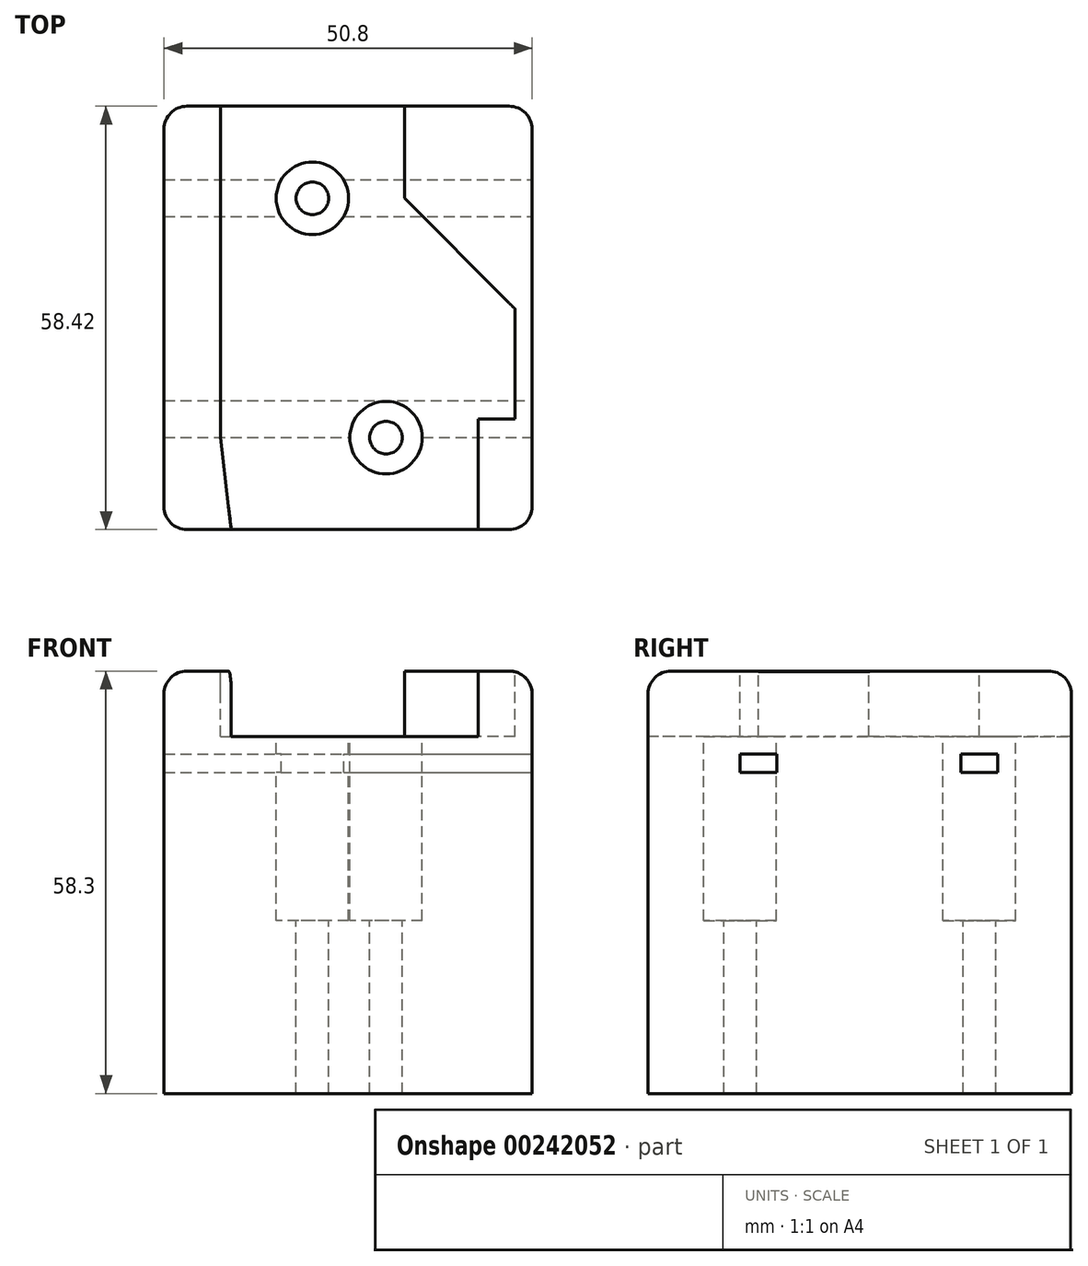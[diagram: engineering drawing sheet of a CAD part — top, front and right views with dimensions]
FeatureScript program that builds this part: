
annotation { "Feature Type Name" : "Feature", "Feature Type Description" : "" }
export const myFeature = defineFeature(function(context is Context, id is Id, definition is map)
    precondition{}
    {
        {
            var Q0;
            Q0=qCreatedBy(makeId("Top.planeOp"),FACE);
            var sketch = newSketch(context, id + "F0", { "sketchPlane" : qUnion([Q0])});
            skLineSegment(sketch, "E0.bottom", {"start": v(3.17, 58.42) * mm, "end": v(47.62, 58.42) * mm});
            skLineSegment(sketch, "E0.top", {"start": v(3.18, 0) * mm, "end": v(47.62, 0) * mm});
            skLineSegment(sketch, "E0.left", {"start": v(0, 55.24) * mm, "end": v(0, 3.17) * mm});
            skLineSegment(sketch, "E0.right", {"start": v(50.8, 55.24) * mm, "end": v(50.8, 3.17) * mm});
            skPoint(sketch, "E1.visualSharp", {"position": v(0, 58.42) * mm});
            skArc(sketch, "E1.filletArc", {"start": v(3.17, 58.42) * mm, "mid": v(0.93, 57.5) * mm, "end": v(0, 55.24) * mm});
            skPoint(sketch, "E2.visualSharp", {"position": v(50.8, 58.42) * mm});
            skArc(sketch, "E2.filletArc", {"start": v(50.8, 55.24) * mm, "mid": v(49.87, 57.5) * mm, "end": v(47.62, 58.42) * mm});
            skPoint(sketch, "E3.visualSharp", {"position": v(50.8, 0) * mm});
            skArc(sketch, "E3.filletArc", {"start": v(47.63, 0) * mm, "mid": v(49.87, 0.93) * mm, "end": v(50.8, 3.17) * mm});
            skPoint(sketch, "E4.visualSharp", {"position": v(0, 0) * mm});
            skArc(sketch, "E4.filletArc", {"start": v(0, 3.17) * mm, "mid": v(0.93, 0.93) * mm, "end": v(3.18, 0) * mm});
            skSolve(sketch);
        }
        {
            var Q0;
            Q0=makeQuery(id+"F0.imprint","IMPRINT",FACE,{"disambiguationData":[TD([[makeQuery(id+"F0.imprint","IMPRINT",EDGE,{"derivedFrom":sQuery(id+"F0.wireOp",EDGE,"E0.bottom")}),-1.0]])]});
            extrude(context, id + "F1", {"entities" : qUnion([Q0]), "depth" : 50.8 * mm + 7.5 * mm});
        }
        {
            var Q0;
            Q0=makeQuery(id+"F1.opExtrude","CAP_FACE",FACE,{"disambiguationData":[OSD([sQuery(id+"F0.wireOp",EDGE,"E0.bottom"),sQuery(id+"F0.wireOp",EDGE,"E0.top"),sQuery(id+"F0.wireOp",EDGE,"E0.left"),sQuery(id+"F0.wireOp",EDGE,"E0.right"),sQuery(id+"F0.wireOp",EDGE,"E1.filletArc"),sQuery(id+"F0.wireOp",EDGE,"E2.filletArc"),sQuery(id+"F0.wireOp",EDGE,"E3.filletArc"),sQuery(id+"F0.wireOp",EDGE,"E4.filletArc")])],"isStart":false});
            var sketch = newSketch(context, id + "F2", { "sketchPlane" : qUnion([Q0])});
            skLineSegment(sketch, "E5", {"start": v(33.18, 58.42) * mm, "end": v(33.18, 45.72) * mm});
            skLineSegment(sketch, "E6", {"start": v(33.18, 45.72) * mm, "end": v(48.42, 30.48) * mm});
            skLineSegment(sketch, "E7", {"start": v(48.42, 30.48) * mm, "end": v(48.42, 15.24) * mm});
            skLineSegment(sketch, "E8", {"start": v(48.42, 15.24) * mm, "end": v(43.34, 15.24) * mm});
            skLineSegment(sketch, "E9", {"start": v(43.34, 15.24) * mm, "end": v(43.34, 0) * mm});
            skLineSegment(sketch, "E10", {"start": v(43.34, 0) * mm, "end": v(7.78, 0) * mm});
            skLineSegment(sketch, "E11", {"start": v(7.78, 0) * mm, "end": v(7.78, 58.42) * mm});
            skLineSegment(sketch, "E12", {"start": v(7.78, 12.7) * mm, "end": v(9.28, 0) * mm});
            skSolve(sketch);
        }
        {
            var Q0;
            {var subQ0=sQuery(id+"F2.wireOp",EDGE,"E5");Q0=makeQuery(id+"F2.imprint","IMPRINT",FACE,{"disambiguationData":[TD([[makeQuery(id+"F2.imprint","IMPRINT",EDGE,{"derivedFrom":subQ0}),-1.0]])]});}
            extrude(context, id + "F3", {"entities" : qUnion([Q0]), "operationType" : NewBodyOperationType.REMOVE, "oppositeDirection" : true, "depth" : 9.02 * mm});
        }
        {
            var Q0;
            Q0=makeQuery(id+"F1.opExtrude","SWEPT_FACE",FACE,{"disambiguationData":[OSD([sQuery(id+"F0.wireOp",EDGE,"E0.right")])]});
            var sketch = newSketch(context, id + "F4", { "sketchPlane" : qUnion([Q0])});
            skLineSegment(sketch, "E13.bottom", {"start": v(12.7, 46.87) * mm, "end": v(17.78, 46.87) * mm});
            skLineSegment(sketch, "E13.top", {"start": v(12.7, 44.33) * mm, "end": v(17.78, 44.33) * mm});
            skLineSegment(sketch, "E13.left", {"start": v(12.7, 46.87) * mm, "end": v(12.7, 44.33) * mm});
            skLineSegment(sketch, "E13.right", {"start": v(17.78, 46.87) * mm, "end": v(17.78, 44.33) * mm});
            skLineSegment(sketch, "E14.bottom", {"start": v(43.18, 44.33) * mm, "end": v(48.26, 44.33) * mm});
            skLineSegment(sketch, "E14.top", {"start": v(43.18, 46.87) * mm, "end": v(48.26, 46.87) * mm});
            skLineSegment(sketch, "E14.left", {"start": v(43.18, 44.33) * mm, "end": v(43.18, 46.87) * mm});
            skLineSegment(sketch, "E14.right", {"start": v(48.26, 44.33) * mm, "end": v(48.26, 46.87) * mm});
            skSolve(sketch);
        }
        {
            var Q0;
            Q0 = qSketchRegion(id + "F4", true);
            extrude(context, id + "F5", {"entities" : qUnion([Q0]), "operationType" : NewBodyOperationType.REMOVE, "endBound" : BoundingType.THROUGH_ALL, "oppositeDirection" : true, "depth" : 25.4 * mm});
        }
        {
            var Q0;
            Q0=makeQuery(id+"F3.boolean.opBoolean","COPY",EDGE,{"derivedFrom":makeQuery(id+"F3.opExtrude","SWEPT_EDGE",EDGE,{"disambiguationData":[OSD([sQuery(id+"F0.wireOp",EDGE,"E0.top"),sQuery(id+"F2.wireOp",EDGE,"E10"),sQuery(id+"F2.wireOp",EDGE,"E11")])]})});
            var Q1;
            Q1=makeQuery(id+"F3.boolean.opBoolean","COPY",EDGE,{"derivedFrom":makeQuery(id+"F3.opExtrude","SWEPT_EDGE",EDGE,{"disambiguationData":[OSD([sQuery(id+"F0.wireOp",EDGE,"E0.top"),sQuery(id+"F2.wireOp",EDGE,"E9"),sQuery(id+"F2.wireOp",EDGE,"E10")])]})});
            var Q2;
            Q2=makeQuery(id+"F3.boolean.opBoolean","COPY",EDGE,{"derivedFrom":makeQuery(id+"F3.opExtrude","SWEPT_EDGE",EDGE,{"disambiguationData":[OSD([sQuery(id+"F0.wireOp",EDGE,"E0.bottom"),sQuery(id+"F2.wireOp",EDGE,"E11")])]})});
            var Q3;
            Q3=makeQuery(id+"F3.boolean.opBoolean","COPY",EDGE,{"derivedFrom":makeQuery(id+"F3.opExtrude","SWEPT_EDGE",EDGE,{"disambiguationData":[OSD([sQuery(id+"F0.wireOp",EDGE,"E0.bottom"),sQuery(id+"F2.wireOp",EDGE,"E5")])]})});
            var Q4;
            Q4=makeQuery(id+"F1.opExtrude","CAP_EDGE",EDGE,{"disambiguationData":[OSD([sQuery(id+"F0.wireOp",EDGE,"E0.left")])],"isStart":false});
            var Q5;
            Q5=makeQuery(id+"F1.opExtrude","CAP_EDGE",EDGE,{"disambiguationData":[OSD([sQuery(id+"F0.wireOp",EDGE,"E0.right")])],"isStart":false});
            var Q6;
            Q6=makeQuery(id+"F3.boolean.opBoolean","COPY",EDGE,{"derivedFrom":makeQuery(id+"F3.opExtrude","SWEPT_EDGE",EDGE,{"disambiguationData":[OSD([sQuery(id+"F2.wireOp",EDGE,"E10"),sQuery(id+"F2.wireOp",EDGE,"E12")])]})});
            fillet(context, id + "F6", {"entities" : qUnion([Q0, Q1, Q2, Q3, Q4, Q5, Q6]), "radius" : 3.17 * mm, "tangentPropagation" : true, "allowEdgeOverflow" : false});
        }
        {
            var Q0;
            Q0=makeQuery(id+"F3.boolean.opBoolean","COPY",FACE,{"derivedFrom":makeQuery(id+"F3.opExtrude","CAP_FACE",FACE,{"disambiguationData":[OSD([sQuery(id+"F0.wireOp",EDGE,"E0.bottom"),sQuery(id+"F2.wireOp",EDGE,"E5"),sQuery(id+"F2.wireOp",EDGE,"E6"),sQuery(id+"F2.wireOp",EDGE,"E7"),sQuery(id+"F2.wireOp",EDGE,"E8"),sQuery(id+"F2.wireOp",EDGE,"E9"),sQuery(id+"F2.wireOp",EDGE,"E10"),sQuery(id+"F2.wireOp",EDGE,"E11")])],"isStart":false})});
            var sketch = newSketch(context, id + "F7", { "sketchPlane" : qUnion([Q0])});
            skCircle(sketch, "E15", {"center": v(30.64, 12.7) * mm, "radius": 5 * mm});
            skCircle(sketch, "E16", {"center": v(20.48, 45.72) * mm, "radius": 5 * mm});
            skSolve(sketch);
        }
        {
            var Q0;
            Q0=makeQuery(id+"F7.imprint","IMPRINT",FACE,{"disambiguationData":[TD([[makeQuery(id+"F7.imprint","IMPRINT",EDGE,{"derivedFrom":sQuery(id+"F7.wireOp",EDGE,"E16")}),1.0]])]});
            var Q1;
            Q1=makeQuery(id+"F7.imprint","IMPRINT",FACE,{"disambiguationData":[TD([[makeQuery(id+"F7.imprint","IMPRINT",EDGE,{"derivedFrom":sQuery(id+"F7.wireOp",EDGE,"E15")}),1.0]])]});
            extrude(context, id + "F8", {"entities" : qUnion([Q0, Q1]), "operationType" : NewBodyOperationType.REMOVE, "oppositeDirection" : true, "depth" : 25.4 * mm});
        }
        {
            var Q0;
            Q0=makeQuery(id+"F3.boolean.opBoolean","COPY",FACE,{"derivedFrom":makeQuery(id+"F3.opExtrude","CAP_FACE",FACE,{"disambiguationData":[OSD([sQuery(id+"F0.wireOp",EDGE,"E0.bottom"),sQuery(id+"F2.wireOp",EDGE,"E5"),sQuery(id+"F2.wireOp",EDGE,"E6"),sQuery(id+"F2.wireOp",EDGE,"E7"),sQuery(id+"F2.wireOp",EDGE,"E8"),sQuery(id+"F2.wireOp",EDGE,"E9"),sQuery(id+"F2.wireOp",EDGE,"E10"),sQuery(id+"F2.wireOp",EDGE,"E11")])],"isStart":false})});
            var sketch = newSketch(context, id + "F9", { "sketchPlane" : qUnion([Q0])});
            skCircle(sketch, "E17", {"center": v(30.64, 12.7) * mm, "radius": 2.25 * mm});
            skCircle(sketch, "E18", {"center": v(20.48, 45.72) * mm, "radius": 2.25 * mm});
            skSolve(sketch);
        }
        {
            var Q0;
            Q0=makeQuery(id+"F9.imprint","IMPRINT",FACE,{"disambiguationData":[TD([[makeQuery(id+"F9.imprint","IMPRINT",EDGE,{"derivedFrom":sQuery(id+"F9.wireOp",EDGE,"E18")}),1.0]])]});
            var Q1;
            Q1=makeQuery(id+"F9.imprint","IMPRINT",FACE,{"disambiguationData":[TD([[makeQuery(id+"F9.imprint","IMPRINT",EDGE,{"derivedFrom":sQuery(id+"F9.wireOp",EDGE,"E17")}),1.0]])]});
            extrude(context, id + "F10", {"entities" : qUnion([Q0, Q1]), "operationType" : NewBodyOperationType.REMOVE, "endBound" : BoundingType.THROUGH_ALL, "oppositeDirection" : true, "depth" : 25.4 * mm});
        }
    });
